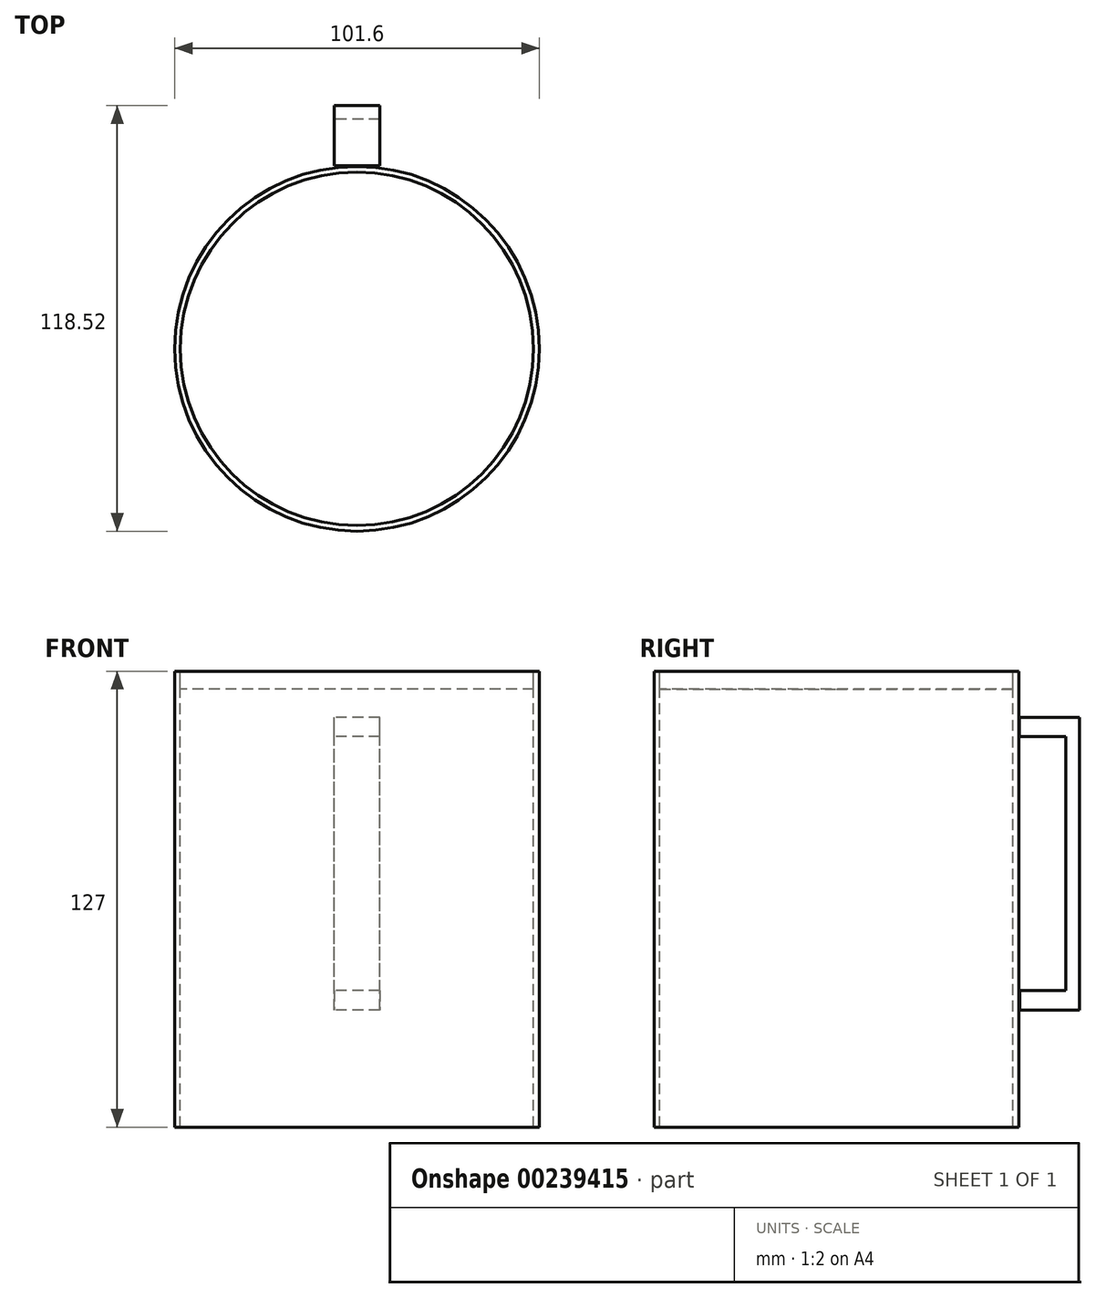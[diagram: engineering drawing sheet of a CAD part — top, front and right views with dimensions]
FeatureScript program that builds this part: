
annotation { "Feature Type Name" : "Feature", "Feature Type Description" : "" }
export const myFeature = defineFeature(function(context is Context, id is Id, definition is map)
    precondition{}
    {
        {
            var Q0;
            Q0=qCreatedBy(makeId("Top.planeOp"),FACE);
            var sketch = newSketch(context, id + "F0", { "sketchPlane" : qUnion([Q0])});
            skCircle(sketch, "E0", {"center": v(0, 0) * mm, "radius": 50.8 * mm});
            skCircle(sketch, "E1", {"center": v(0, 0) * mm, "radius": 49.21 * mm});
            skSolve(sketch);
        }
        {
            var Q0;
            Q0 = qSketchRegion(id + "F0", true);
            extrude(context, id + "F1", {"entities" : qUnion([Q0]), "oppositeDirection" : true, "depth" : 127 * mm});
        }
        {
            var Q0;
            Q0=makeQuery(id+"F0.imprint","IMPRINT",FACE,{"disambiguationData":[TD([[makeQuery(id+"F0.imprint","IMPRINT",EDGE,{"derivedFrom":sQuery(id+"F0.wireOp",EDGE,"E1")}),1.0]])]});
            extrude(context, id + "F2", {"entities" : qUnion([Q0]), "oppositeDirection" : true, "depth" : 4.98 * mm});
        }
        {
            var Q0;
            Q0=qCreatedBy(makeId("Right.planeOp"),FACE);
            var sketch = newSketch(context, id + "F3", { "sketchPlane" : qUnion([Q0])});
            skLineSegment(sketch, "E2.bottom", {"start": v(67.72, -88.98) * mm, "end": v(63.94, -88.98) * mm});
            skLineSegment(sketch, "E2.top", {"start": v(67.72, -18.22) * mm, "end": v(63.94, -18.22) * mm});
            skLineSegment(sketch, "E2.left", {"start": v(67.72, -88.98) * mm, "end": v(67.72, -18.22) * mm});
            skLineSegment(sketch, "E2.right", {"start": v(63.94, -88.98) * mm, "end": v(63.94, -18.22) * mm});
            skLineSegment(sketch, "E3.bottom", {"start": v(67.72, -18.22) * mm, "end": v(50.97, -18.22) * mm});
            skLineSegment(sketch, "E3.top", {"start": v(67.72, -12.86) * mm, "end": v(50.97, -12.86) * mm});
            skLineSegment(sketch, "E3.left", {"start": v(67.72, -18.22) * mm, "end": v(67.72, -12.86) * mm});
            skLineSegment(sketch, "E3.right", {"start": v(50.97, -18.22) * mm, "end": v(50.97, -12.86) * mm});
            skLineSegment(sketch, "E4.bottom", {"start": v(67.72, -88.98) * mm, "end": v(51.02, -88.98) * mm});
            skLineSegment(sketch, "E4.top", {"start": v(67.72, -94.4) * mm, "end": v(51.02, -94.4) * mm});
            skLineSegment(sketch, "E4.left", {"start": v(67.72, -88.98) * mm, "end": v(67.72, -94.4) * mm});
            skLineSegment(sketch, "E4.right", {"start": v(51.02, -88.98) * mm, "end": v(51.02, -94.4) * mm});
            skSolve(sketch);
        }
        {
            var Q0;
            Q0=makeQuery(id+"F3.imprint","IMPRINT",FACE,{"disambiguationData":[TD([[makeQuery(id+"F3.imprint","IMPRINT",EDGE,{"derivedFrom":sQuery(id+"F3.wireOp",EDGE,"E3.top")}),1.0]])]});
            var Q1;
            {var subQ0=sQuery(id+"F3.wireOp",EDGE,"E2.left");Q1=makeQuery(id+"F3.imprint","IMPRINT",FACE,{"disambiguationData":[TD([[makeQuery(id+"F3.imprint","IMPRINT",EDGE,{"derivedFrom":subQ0}),1.0]])]});}
            var Q2;
            Q2=makeQuery(id+"F3.imprint","IMPRINT",FACE,{"disambiguationData":[TD([[makeQuery(id+"F3.imprint","IMPRINT",EDGE,{"derivedFrom":sQuery(id+"F3.wireOp",EDGE,"E4.top")}),-1.0]])]});
            extrude(context, id + "F4", {"entities" : qUnion([Q0, Q1, Q2]), "endBound" : BoundingType.SYMMETRIC, "depth" : 12.7 * mm});
        }
    });
